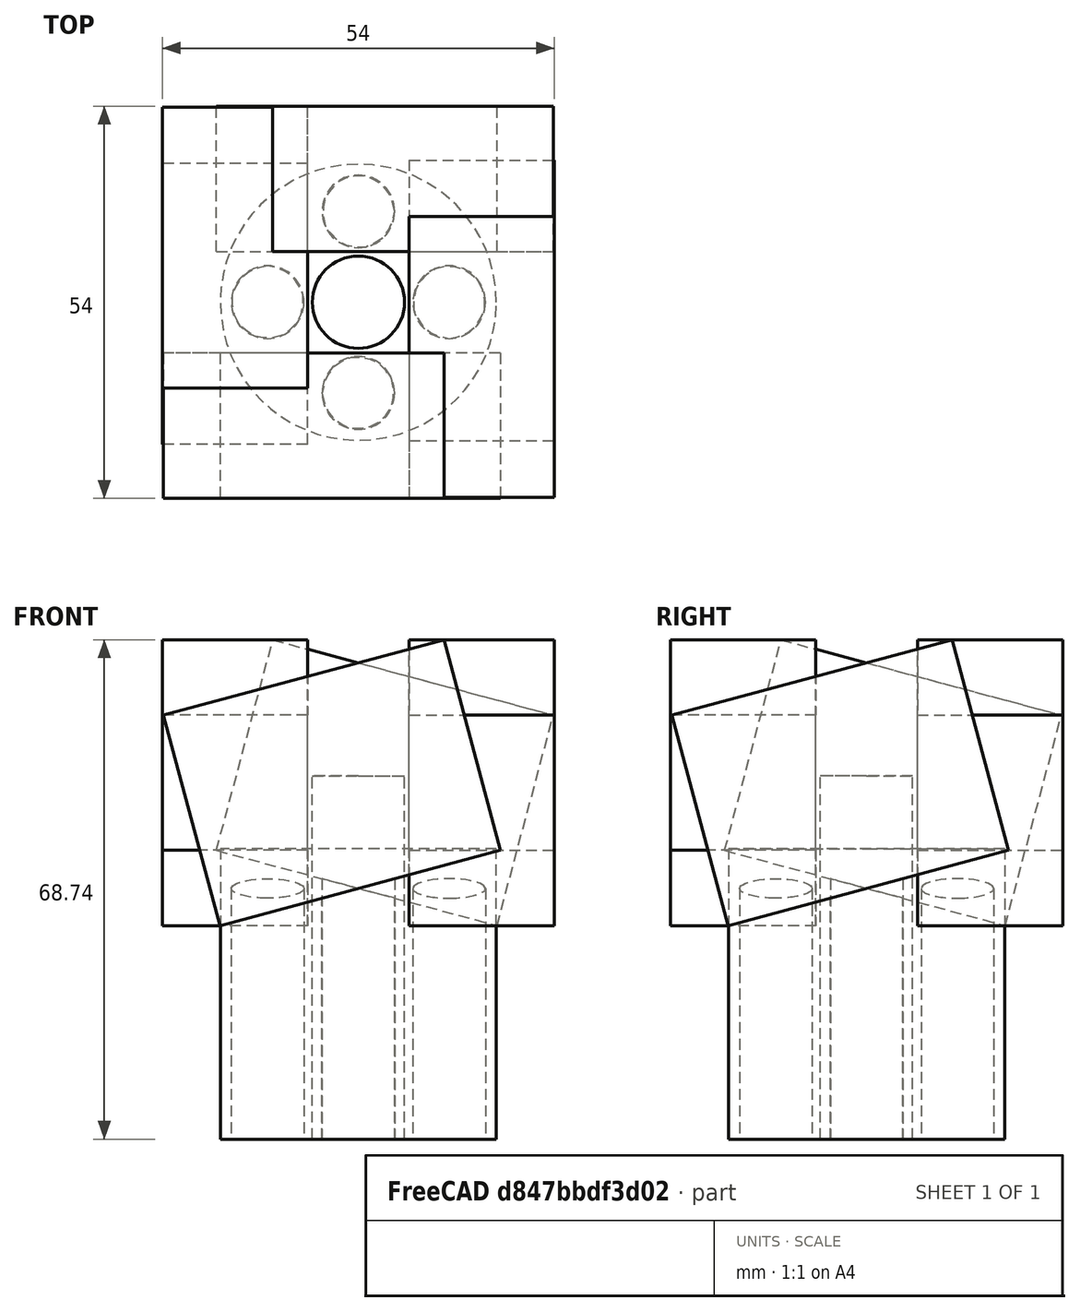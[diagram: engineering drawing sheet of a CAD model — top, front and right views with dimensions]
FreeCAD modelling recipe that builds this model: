
FCSTD DOCUMENT  (FreeCAD 0.20R29410 (Git))
Label: laddleFour1
License: All rights reserved
LicenseURL: http://en.wikipedia.org/wiki/All_rights_reserved
objects: Part::Cylinder×10, Part::MultiFuse×10, Part::Box×4
note: 24 computed .brp shape members not serialized (recipe doc carries the construction recipe); baked Part::Feature solids carry a one-line shape summary decoded from their .brp

FEATURE [Part::Cylinder] Cylinder
  Angle = 360
  AttacherType = Attacher::AttachEngine3D
  FirstAngle = 0
  Height = 40
  Radius = 19
  SecondAngle = 0
FEATURE [Part::Cylinder] Cylinder001
  Angle = 360
  AttacherType = Attacher::AttachEngine3D
  FirstAngle = 0
  Height = 50
  Placement = pos=(0,12.5,0) rot=(0,0,1;0rad)
  Radius = 5
  SecondAngle = 0
FEATURE [Part::Cylinder] Cylinder003  label="bevilPin"
  Angle = 360
  AttacherType = Attacher::AttachEngine3D
  FirstAngle = 0
  Height = 50
  Radius = 6.35
  SecondAngle = 0
FEATURE [Part::Cylinder] Cylinder004  label="bevilPin001"
  Angle = 360
  AttacherType = Attacher::AttachEngine3D
  FirstAngle = 0
  Height = 50
  Radius = 6.35
  SecondAngle = 0
FEATURE [Part::Box] Box  label="Cube"
  AttacherType = Attacher::AttachEngine3D
  Height = 30
  Length = 40
  Placement = pos=(-19.5582,7,39.7598) rot=(0,1,0;0.261799rad)
  Width = 20
FEATURE [Part::MultiFuse] Fusion
  Shapes = -> [Cylinder001,Box]
FEATURE [Part::MultiFuse] Fusion001
  Shapes = -> [Fusion,Cylinder004]
FEATURE [Part::Box] Box001  label="Cube001"
  AttacherType = Attacher::AttachEngine3D
  Height = 30
  Length = 40
  Placement = pos=(-19.5582,7,39.7598) rot=(0,1,0;0.261799rad)
  Width = 20
FEATURE [Part::Cylinder] Cylinder005
  Angle = 360
  AttacherType = Attacher::AttachEngine3D
  FirstAngle = 0
  Height = 50
  Placement = pos=(0,12.5,0) rot=(0,0,1;0rad)
  Radius = 5
  SecondAngle = 0
FEATURE [Part::Cylinder] Cylinder006  label="bevilPin002"
  Angle = 360
  AttacherType = Attacher::AttachEngine3D
  FirstAngle = 0
  Height = 50
  Radius = 6.35
  SecondAngle = 0
FEATURE [Part::MultiFuse] Fusion002
  Shapes = -> [Cylinder005,Box001]
FEATURE [Part::MultiFuse] Fusion003
  Placement = pos=(0,0,0) rot=(0,0,1;3.14159rad)
  Shapes = -> [Fusion002,Cylinder006]
FEATURE [Part::MultiFuse] Fusion004
  Shapes = -> [Fusion003,Fusion001]
FEATURE [Part::Box] Box002  label="Cube002"
  AttacherType = Attacher::AttachEngine3D
  Height = 30
  Length = 40
  Placement = pos=(-19.5582,7,39.7598) rot=(0,1,0;0.261799rad)
  Width = 20
FEATURE [Part::Box] Box003  label="Cube003"
  AttacherType = Attacher::AttachEngine3D
  Height = 30
  Length = 40
  Placement = pos=(-19.5582,7,39.7598) rot=(0,1,0;0.261799rad)
  Width = 20
FEATURE [Part::Cylinder] Cylinder007
  Angle = 360
  AttacherType = Attacher::AttachEngine3D
  FirstAngle = 0
  Height = 50
  Placement = pos=(0,12.5,0) rot=(0,0,1;0rad)
  Radius = 5
  SecondAngle = 0
FEATURE [Part::Cylinder] Cylinder008  label="bevilPin003"
  Angle = 360
  AttacherType = Attacher::AttachEngine3D
  FirstAngle = 0
  Height = 50
  Radius = 6.35
  SecondAngle = 0
FEATURE [Part::Cylinder] Cylinder009
  Angle = 360
  AttacherType = Attacher::AttachEngine3D
  FirstAngle = 0
  Height = 50
  Placement = pos=(0,12.5,0) rot=(0,0,1;0rad)
  Radius = 5
  SecondAngle = 0
FEATURE [Part::Cylinder] Cylinder010  label="bevilPin004"
  Angle = 360
  AttacherType = Attacher::AttachEngine3D
  FirstAngle = 0
  Height = 50
  Radius = 6.35
  SecondAngle = 0
FEATURE [Part::MultiFuse] Fusion005
  Shapes = -> [Cylinder007,Box002]
FEATURE [Part::MultiFuse] Fusion006
  Shapes = -> [Fusion005,Cylinder008]
FEATURE [Part::MultiFuse] Fusion007
  Shapes = -> [Cylinder009,Box003]
FEATURE [Part::MultiFuse] Fusion008
  Placement = pos=(0,0,0) rot=(0,0,1;3.14159rad)
  Shapes = -> [Fusion007,Cylinder010]
FEATURE [Part::MultiFuse] Fusion009
  Placement = pos=(0,0,0) rot=(0,0,-1;1.5708rad)
  Shapes = -> [Fusion008,Fusion006]
